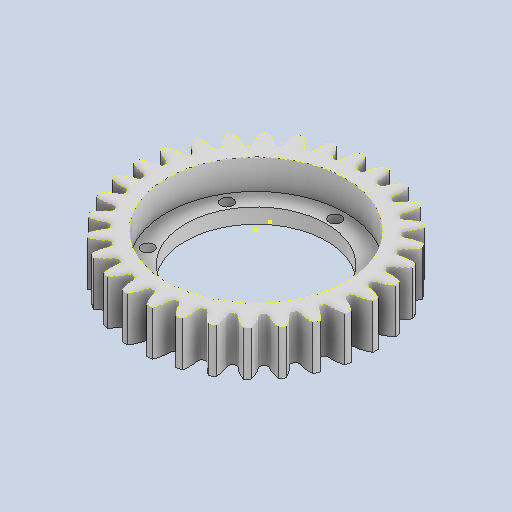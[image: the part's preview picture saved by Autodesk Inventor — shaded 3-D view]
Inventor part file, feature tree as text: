
AUTODESK INVENTOR PART (.ipt)
format: ipt  version: 2024 (Build 280153000, 153)  size: 602,112 bytes
history: native  units: mm
features: sketch x5, extrude x3, pattern_circular x1
ambient origin geometry x8: Origin, YZ Plane, XZ Plane, XY Plane, X Axis, Y Axis, Z Axis, Center Point
bodies: Solid1 (feature_tree)
feature tree (9):
  extrude  "Extrusion1"  Depth=30.0mm TaperAngle=0.0deg
  extrude  "Extrusion2"  Depth=20.0mm TaperAngle=0.0deg
  sketch  "Sketch3"  dims[d11=30.0mm d12=0.0mm d13=300.0mm d14=360.0deg]
  extrude  "Extrusion3"  Depth=300.0mm TaperAngle=360.0deg
  pattern_circular  "Circular Pattern1"  [2 undecoded]
  sketch  "Sketch5"
  sketch  "Sketch1"  dims[d1=60.0mm d2=125.0mm d3=106.0mm d4=360.0deg d5=8.1mm d6=30.0mm d7=0.0mm]
  sketch  "Sketch2"  dims[d8=120.000028mm d9=20.0mm d10=0.0mm]
  sketch  "Sketch4"
note: 2 required parameter values undecoded (feature->parameter linkage not recoverable at this tier; creation-order binding heuristic only, values carry confidence <= 0.55)
